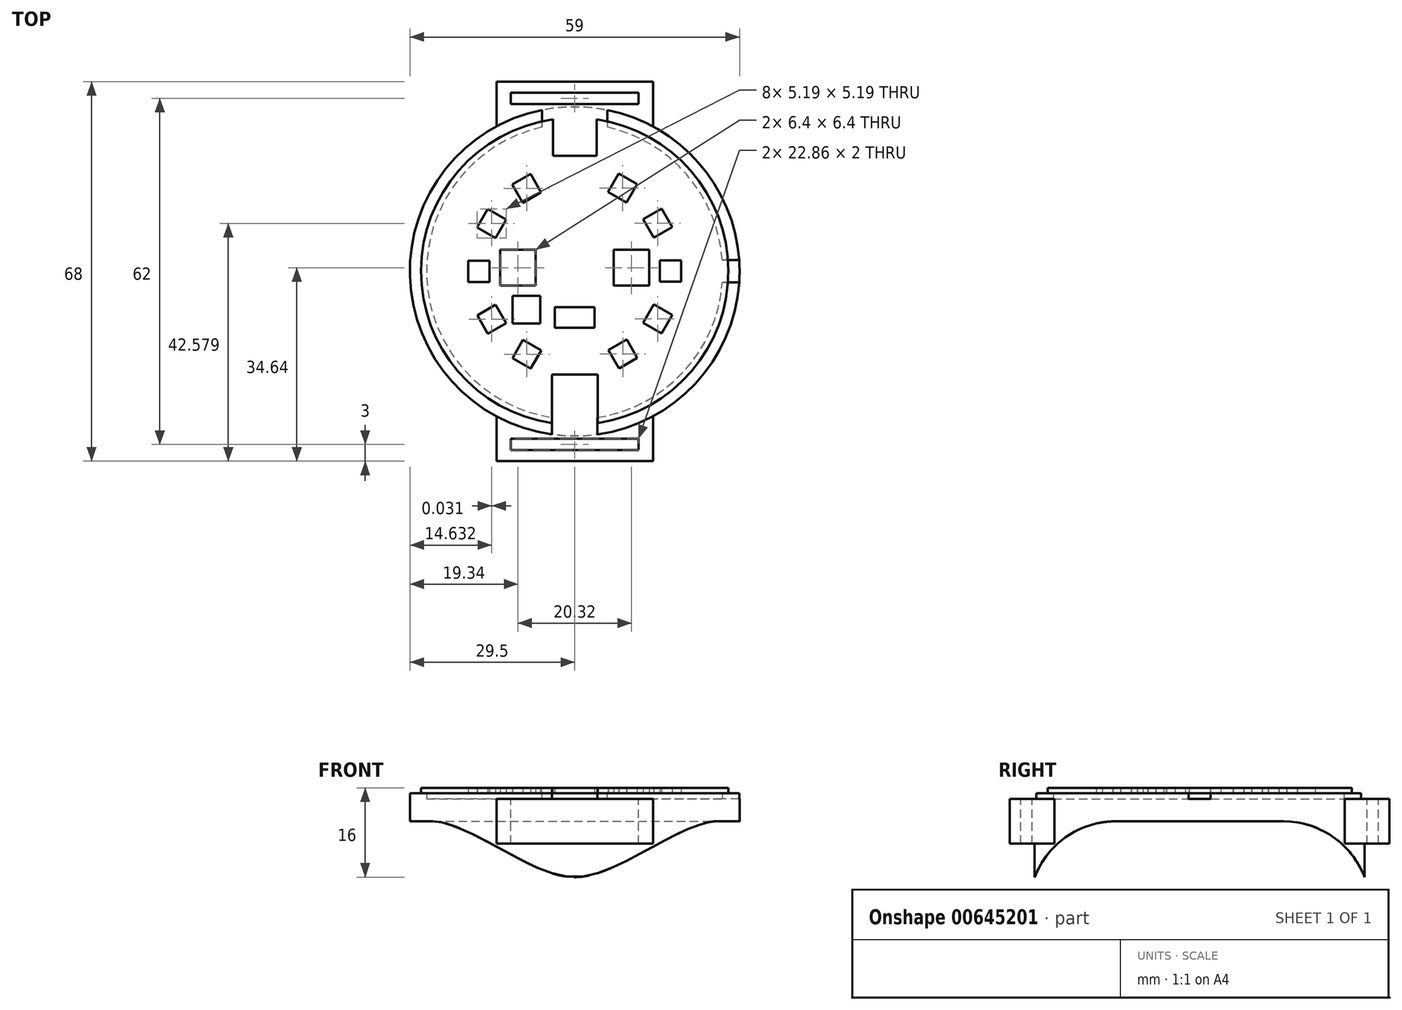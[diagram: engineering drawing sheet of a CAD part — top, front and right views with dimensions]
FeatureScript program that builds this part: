
annotation { "Feature Type Name" : "Feature", "Feature Type Description" : "" }
export const myFeature = defineFeature(function(context is Context, id is Id, definition is map)
    precondition{}
    {
        {
            var Q0;
            Q0=qCreatedBy(makeId("Top.planeOp"),FACE);
            var sketch = newSketch(context, id + "F0", { "sketchPlane" : qUnion([Q0])});
            skCircle(sketch, "E0", {"center": v(0, 0) * mm, "radius": 26.5 * mm});
            skCircle(sketch, "E1.0", {"center": v(0, 0) * mm, "radius": 29.5 * mm});
            skSolve(sketch);
        }
        {
            var Q0;
            Q0=makeQuery(id+"F0.imprint","IMPRINT",FACE,{"disambiguationData":[TD([[makeQuery(id+"F0.imprint","IMPRINT",EDGE,{"derivedFrom":sQuery(id+"F0.wireOp",EDGE,"E0")}),-1.0]])]});
            var Q1;
            Q1=makeQuery(id+"F0.imprint","IMPRINT",FACE,{"disambiguationData":[TD([[makeQuery(id+"F0.imprint","IMPRINT",EDGE,{"derivedFrom":sQuery(id+"F0.wireOp",EDGE,"E0")}),1.0]])]});
            var Q2;
            Q2 = qConstructionFilter(qBodyType(qCreatedBy(id + "F0" ,EDGE), BodyType.WIRE), ConstructionObject.NO);
            extrude(context, id + "F1", {"entities" : qUnion([Q0, Q1]), "surfaceEntities" : qUnion([Q2]), "oppositeDirection" : true, "depth" : 4 * mm, "offsetDistance" : 25 * mm});
        }
        {
            var Q0;
            Q0=makeQuery(id+"F1.opExtrude","CAP_FACE",FACE,{"disambiguationData":[OSD([sQuery(id+"F0.wireOp",EDGE,"E1.0")])],"isStart":false});
            var sketch = newSketch(context, id + "F2", { "sketchPlane" : qUnion([Q0])});
            skLineSegment(sketch, "E2", {"start": v(0, 29.5) * mm, "end": v(0, -29.5) * mm});
            skSolve(sketch);
        }
        {
            var Q0;
            Q0=makeQuery(id+"F0.imprint","IMPRINT",FACE,{"disambiguationData":[TD([[makeQuery(id+"F0.imprint","IMPRINT",EDGE,{"derivedFrom":sQuery(id+"F0.wireOp",EDGE,"E0")}),-1.0]])]});
            extrude(context, id + "F3", {"entities" : qUnion([Q0]), "operationType" : NewBodyOperationType.ADD, "depth" : 1 * mm, "offsetDistance" : 25 * mm});
        }
        {
            var Q0;
            Q0=qCreatedBy(makeId("Front.planeOp"),FACE);
            var sketch = newSketch(context, id + "F4", { "sketchPlane" : qUnion([Q0])});
            skLineSegment(sketch, "E3", {"start": v(0, 0) * mm, "end": v(-4.05, 0) * mm});
            skLineSegment(sketch, "E4.MirrorCS", {"start": v(0, 0) * mm, "end": v(4.05, 0) * mm});
            skLineSegment(sketch, "E5", {"start": v(-4.05, 0) * mm, "end": v(-4.05, 3) * mm});
            skLineSegment(sketch, "E6", {"start": v(-4.05, 3) * mm, "end": v(4.05, 3) * mm});
            skLineSegment(sketch, "E7", {"start": v(4.05, 3) * mm, "end": v(4.05, 0) * mm});
            skSolve(sketch);
        }
        {
            var Q0;
            Q0 = qSketchRegion(id + "F4", true);
            extrude(context, id + "F5", {"entities" : qUnion([Q0]), "operationType" : NewBodyOperationType.REMOVE, "endBound" : BoundingType.THROUGH_ALL, "depth" : 25 * mm, "offsetDistance" : 25 * mm});
        }
        {
            var Q0;
            Q0=qCreatedBy(makeId("Front.planeOp"),FACE);
            var sketch = newSketch(context, id + "F6", { "sketchPlane" : qUnion([Q0])});
            skLineSegment(sketch, "E8", {"start": v(0, 0) * mm, "end": v(-5.85, 0) * mm});
            skLineSegment(sketch, "E9.MirrorCS", {"start": v(0, 0) * mm, "end": v(5.85, 0) * mm});
            skLineSegment(sketch, "E10", {"start": v(-5.85, 0) * mm, "end": v(-5.85, 3) * mm});
            skLineSegment(sketch, "E11", {"start": v(-5.85, 3) * mm, "end": v(5.85, 3) * mm});
            skLineSegment(sketch, "E12", {"start": v(5.85, 3) * mm, "end": v(5.85, 0) * mm});
            skSolve(sketch);
        }
        {
            var Q0;
            Q0 = qSketchRegion(id + "F6", true);
            extrude(context, id + "F7", {"entities" : qUnion([Q0]), "operationType" : NewBodyOperationType.REMOVE, "endBound" : BoundingType.THROUGH_ALL, "oppositeDirection" : true, "depth" : 25 * mm, "offsetDistance" : 25 * mm});
        }
        {
            var Q0;
            Q0=qCreatedBy(makeId("Front.planeOp"),FACE);
            var sketch = newSketch(context, id + "F8", { "sketchPlane" : qUnion([Q0])});
            skLineSegment(sketch, "E13", {"start": v(0, 0) * mm, "end": v(-14, 0) * mm});
            skLineSegment(sketch, "E14.MirrorCS", {"start": v(0, 0) * mm, "end": v(14, 0) * mm});
            skLineSegment(sketch, "E15", {"start": v(-14, 0) * mm, "end": v(-14, -4) * mm});
            skLineSegment(sketch, "E16", {"start": v(-14, -4) * mm, "end": v(14, -4) * mm});
            skLineSegment(sketch, "E17", {"start": v(14, -4) * mm, "end": v(14, 0) * mm});
            skSolve(sketch);
        }
        {
            var Q0;
            Q0 = qSketchRegion(id + "F8", true);
            var Q1;
            {var subQ0=sQuery(id+"F0.wireOp",EDGE,"E1.0");Q1=makeQuery(id+"F3.boolean.opBoolean","MERGE",FACE,{"derivedFrom":[makeQuery(id+"F1.opExtrude","SWEPT_FACE",FACE,{"disambiguationData":[OSD([subQ0])]}),makeQuery(id+"F3.opExtrude","SWEPT_FACE",FACE,{"disambiguationData":[OSD([subQ0])]})]});}
            extrude(context, id + "F9", {"entities" : qUnion([Q0]), "operationType" : NewBodyOperationType.ADD, "endBound" : BoundingType.SYMMETRIC, "depth" : 68 * mm, "endBoundEntityFace" : qUnion([Q1]), "offsetDistance" : 25 * mm});
        }
        {
            var Q0;
            Q0=makeQuery(id+"F9.boolean.opBoolean","MERGE",FACE,{"derivedFrom":[makeQuery(id+"F7.boolean.opBoolean","MERGE",FACE,{"derivedFrom":[makeQuery(id+"F5.boolean.opBoolean","MERGE",FACE,{"derivedFrom":[makeQuery(id+"F1.opExtrude","CAP_FACE",FACE,{"disambiguationData":[OSD([sQuery(id+"F0.wireOp",EDGE,"E1.0")])],"isStart":true}),makeQuery(id+"F5.opExtrude","SWEPT_FACE",FACE,{"disambiguationData":[OSD([sQuery(id+"F4.wireOp",EDGE,"E3"),sQuery(id+"F4.wireOp",EDGE,"E4.MirrorCS")])]})]}),makeQuery(id+"F7.opExtrude","SWEPT_FACE",FACE,{"disambiguationData":[OSD([sQuery(id+"F6.wireOp",EDGE,"E8"),sQuery(id+"F6.wireOp",EDGE,"E9.MirrorCS")])]})]}),makeQuery(id+"F9.opExtrude","SWEPT_FACE",FACE,{"disambiguationData":[OSD([sQuery(id+"F8.wireOp",EDGE,"E13"),sQuery(id+"F8.wireOp",EDGE,"E14.MirrorCS")])]})]});
            var sketch = newSketch(context, id + "F10", { "sketchPlane" : qUnion([Q0])});
            skLineSegment(sketch, "E18", {"start": v(0, 0) * mm, "end": v(0, -31) * mm, "construction": true});
            skLineSegment(sketch, "E19.bottom", {"start": v(11.43, -30) * mm, "end": v(-11.43, -30) * mm});
            skLineSegment(sketch, "E19.top", {"start": v(11.43, -32) * mm, "end": v(-11.43, -32) * mm});
            skLineSegment(sketch, "E19.left", {"start": v(11.43, -30) * mm, "end": v(11.43, -32) * mm});
            skLineSegment(sketch, "E19.right", {"start": v(-11.43, -30) * mm, "end": v(-11.43, -32) * mm});
            skPoint(sketch, "E19.middle", {"position": v(0, -31) * mm});
            skLineSegment(sketch, "E20.MirrorCS", {"start": v(11.43, 32) * mm, "end": v(-11.43, 32) * mm});
            skLineSegment(sketch, "E21.MirrorCS", {"start": v(11.43, 30) * mm, "end": v(-11.43, 30) * mm});
            skLineSegment(sketch, "E22.MirrorCS", {"start": v(11.43, 30) * mm, "end": v(11.43, 32) * mm});
            skLineSegment(sketch, "E23.MirrorCS", {"start": v(-11.43, 30) * mm, "end": v(-11.43, 32) * mm});
            skSolve(sketch);
        }
        {
            var Q0;
            Q0=makeQuery(id+"F10.imprint","IMPRINT",FACE,{"disambiguationData":[TD([[makeQuery(id+"F10.imprint","IMPRINT",EDGE,{"derivedFrom":sQuery(id+"F10.wireOp",EDGE,"E20.MirrorCS")}),1.0]])]});
            var Q1;
            Q1=makeQuery(id+"F10.imprint","IMPRINT",FACE,{"disambiguationData":[TD([[makeQuery(id+"F10.imprint","IMPRINT",EDGE,{"derivedFrom":sQuery(id+"F10.wireOp",EDGE,"E19.bottom")}),1.0]])]});
            extrude(context, id + "F11", {"entities" : qUnion([Q0, Q1]), "operationType" : NewBodyOperationType.REMOVE, "endBound" : BoundingType.THROUGH_ALL, "oppositeDirection" : true, "depth" : 25 * mm, "offsetDistance" : 25 * mm});
        }
        {
            var Q0;
            Q0=qCreatedBy(makeId("Right.planeOp"),FACE);
            var sketch = newSketch(context, id + "F12", { "sketchPlane" : qUnion([Q0])});
            skLineSegment(sketch, "E24", {"start": v(0, 0) * mm, "end": v(-2, 0) * mm});
            skLineSegment(sketch, "E25", {"start": v(-2, 0) * mm, "end": v(-2, 3) * mm});
            skLineSegment(sketch, "E26", {"start": v(-2, 3) * mm, "end": v(0, 3) * mm});
            skLineSegment(sketch, "E27.MirrorCS", {"start": v(2, 0) * mm, "end": v(2, 3) * mm});
            skLineSegment(sketch, "E28.MirrorCS", {"start": v(0, 0) * mm, "end": v(2, 0) * mm});
            skLineSegment(sketch, "E29.MirrorCS", {"start": v(2, 3) * mm, "end": v(0, 3) * mm});
            skSolve(sketch);
        }
        {
            var Q0;
            Q0 = qSketchRegion(id + "F12", true);
            extrude(context, id + "F13", {"entities" : qUnion([Q0]), "operationType" : NewBodyOperationType.REMOVE, "endBound" : BoundingType.THROUGH_ALL, "depth" : 25 * mm, "offsetDistance" : 25 * mm});
        }
        {
            var Q0;
            {var subQ0=makeQuery(id+"F5.boolean.opBoolean","COPY",FACE,{"derivedFrom":makeQuery(id+"F5.opExtrude","SWEPT_FACE",FACE,{"disambiguationData":[OSD([sQuery(id+"F4.wireOp",EDGE,"E7")])]})});var subQ1=sQuery(id+"F0.wireOp",EDGE,"E0");var subQ3=sQuery(id+"F0.wireOp",EDGE,"E1.0");Q0=makeQuery(id+"F13.boolean.opBoolean","SPLIT",FACE,{"disambiguationData":[TD([subQ0])],"derivedFrom":makeQuery(id+"F7.boolean.opBoolean","SPLIT",FACE,{"disambiguationData":[TD([subQ0])],"derivedFrom":makeQuery(id+"F3.opExtrude","CAP_FACE",FACE,{"disambiguationData":[OSD([subQ1,subQ3])],"isStart":false})})});}
            var sketch = newSketch(context, id + "F14", { "sketchPlane" : qUnion([Q0])});
            skCircle(sketch, "E30", {"center": v(0, 0) * mm, "radius": 27.5 * mm});
            skSolve(sketch);
        }
        {
            var Q0;
            {var subQ0=sQuery(id+"F0.wireOp",EDGE,"E1.0");var subQ1=sQuery(id+"F0.wireOp",EDGE,"E0");Q0=makeQuery(id+"F7.boolean.opBoolean","SPLIT",FACE,{"disambiguationData":[TD([makeQuery(id+"F5.boolean.opBoolean","COPY",FACE,{"derivedFrom":makeQuery(id+"F5.opExtrude","SWEPT_FACE",FACE,{"disambiguationData":[OSD([sQuery(id+"F4.wireOp",EDGE,"E5")])]})})])],"derivedFrom":makeQuery(id+"F3.opExtrude","CAP_FACE",FACE,{"disambiguationData":[OSD([subQ1,subQ0])],"isStart":false})});}
            var sketch = newSketch(context, id + "F15", { "sketchPlane" : qUnion([Q0])});
            skLineSegment(sketch, "E31.bottom", {"start": v(-15.25, 1.9) * mm, "end": v(-19.05, 1.9) * mm});
            skLineSegment(sketch, "E31.top", {"start": v(-15.25, -1.9) * mm, "end": v(-19.05, -1.9) * mm});
            skLineSegment(sketch, "E31.left", {"start": v(-15.25, 1.9) * mm, "end": v(-15.25, -1.9) * mm});
            skLineSegment(sketch, "E31.right", {"start": v(-19.05, 1.9) * mm, "end": v(-19.05, -1.9) * mm});
            skPoint(sketch, "E31.middle", {"position": v(-17.15, 0) * mm});
            skLineSegment(sketch, "E32", {"start": v(0, 0) * mm, "end": v(0, 0.64) * mm, "construction": true});
            skLineSegment(sketch, "E33.bottom", {"start": v(-6.96, 3.84) * mm, "end": v(-13.36, 3.84) * mm});
            skLineSegment(sketch, "E33.top", {"start": v(-6.96, -2.56) * mm, "end": v(-13.36, -2.56) * mm});
            skLineSegment(sketch, "E33.left", {"start": v(-6.96, 3.84) * mm, "end": v(-6.96, -2.56) * mm});
            skLineSegment(sketch, "E33.right", {"start": v(-13.36, 3.84) * mm, "end": v(-13.36, -2.56) * mm});
            skPoint(sketch, "E33.middle", {"position": v(-10.16, 0.64) * mm});
            skLineSegment(sketch, "E34.bottom", {"start": v(-11.14, -4.36) * mm, "end": v(-6.14, -4.36) * mm});
            skLineSegment(sketch, "E34.top", {"start": v(-11.14, -9.36) * mm, "end": v(-6.14, -9.36) * mm});
            skLineSegment(sketch, "E34.left", {"start": v(-11.14, -4.36) * mm, "end": v(-11.14, -9.36) * mm});
            skLineSegment(sketch, "E34.right", {"start": v(-6.14, -4.36) * mm, "end": v(-6.14, -9.36) * mm});
            skPoint(sketch, "E34.middle", {"position": v(-8.64, -6.86) * mm});
            skLineSegment(sketch, "E35.bottom", {"start": v(3.55, -6.44) * mm, "end": v(-3.55, -6.44) * mm});
            skLineSegment(sketch, "E35.top", {"start": v(3.55, -10.09) * mm, "end": v(-3.55, -10.09) * mm});
            skLineSegment(sketch, "E35.left", {"start": v(3.55, -6.44) * mm, "end": v(3.55, -10.09) * mm});
            skLineSegment(sketch, "E35.right", {"start": v(-3.55, -6.44) * mm, "end": v(-3.55, -10.08) * mm});
            skPoint(sketch, "E35.middle", {"position": v(0, -8.26) * mm});
            skLineSegment(sketch, "E36.MirrorCS", {"start": v(6.96, 3.84) * mm, "end": v(13.36, 3.84) * mm});
            skLineSegment(sketch, "E37.MirrorCS", {"start": v(13.36, 3.84) * mm, "end": v(13.36, -2.56) * mm});
            skLineSegment(sketch, "E38.MirrorCS", {"start": v(6.96, -2.56) * mm, "end": v(13.36, -2.56) * mm});
            skLineSegment(sketch, "E39.MirrorCS", {"start": v(6.96, 3.84) * mm, "end": v(6.96, -2.56) * mm});
            skLineSegment(sketch, "E40.1.0", {"start": v(-17.43, -7.88) * mm, "end": v(-15.53, -11.17) * mm});
            skLineSegment(sketch, "E40.1.1", {"start": v(-12.24, -9.27) * mm, "end": v(-15.53, -11.17) * mm});
            skLineSegment(sketch, "E40.1.2", {"start": v(-14.14, -5.98) * mm, "end": v(-17.43, -7.88) * mm});
            skLineSegment(sketch, "E40.1.3", {"start": v(-14.14, -5.98) * mm, "end": v(-12.24, -9.27) * mm});
            skLineSegment(sketch, "E40.2.0", {"start": v(-11.14, -15.53) * mm, "end": v(-7.85, -17.43) * mm});
            skLineSegment(sketch, "E40.2.1", {"start": v(-5.95, -14.14) * mm, "end": v(-7.85, -17.43) * mm});
            skLineSegment(sketch, "E40.2.2", {"start": v(-9.24, -12.24) * mm, "end": v(-11.14, -15.53) * mm});
            skLineSegment(sketch, "E40.2.3", {"start": v(-9.24, -12.24) * mm, "end": v(-5.95, -14.14) * mm});
            skLineSegment(sketch, "E40.4.0", {"start": v(7.9, -17.4) * mm, "end": v(11.2, -15.5) * mm});
            skLineSegment(sketch, "E40.4.1", {"start": v(9.3, -12.21) * mm, "end": v(11.2, -15.5) * mm});
            skLineSegment(sketch, "E40.4.2", {"start": v(6, -14.11) * mm, "end": v(7.9, -17.4) * mm});
            skLineSegment(sketch, "E40.4.3", {"start": v(6, -14.11) * mm, "end": v(9.3, -12.21) * mm});
            skLineSegment(sketch, "E40.5.0", {"start": v(15.56, -11.11) * mm, "end": v(17.46, -7.82) * mm});
            skLineSegment(sketch, "E40.5.1", {"start": v(14.17, -5.92) * mm, "end": v(17.46, -7.82) * mm});
            skLineSegment(sketch, "E40.5.2", {"start": v(12.27, -9.21) * mm, "end": v(15.56, -11.11) * mm});
            skLineSegment(sketch, "E40.5.3", {"start": v(12.27, -9.21) * mm, "end": v(14.17, -5.92) * mm});
            skLineSegment(sketch, "E40.6.0", {"start": v(19.05, -1.84) * mm, "end": v(19.05, 1.96) * mm});
            skLineSegment(sketch, "E40.6.1", {"start": v(15.25, 1.96) * mm, "end": v(19.05, 1.96) * mm});
            skLineSegment(sketch, "E40.6.2", {"start": v(15.25, -1.84) * mm, "end": v(19.05, -1.84) * mm});
            skLineSegment(sketch, "E40.6.3", {"start": v(15.25, -1.84) * mm, "end": v(15.25, 1.96) * mm});
            skLineSegment(sketch, "E40.7.0", {"start": v(17.43, 7.94) * mm, "end": v(15.53, 11.23) * mm});
            skLineSegment(sketch, "E40.7.1", {"start": v(12.24, 9.33) * mm, "end": v(15.53, 11.23) * mm});
            skLineSegment(sketch, "E40.7.2", {"start": v(14.14, 6.04) * mm, "end": v(17.43, 7.94) * mm});
            skLineSegment(sketch, "E40.7.3", {"start": v(14.14, 6.04) * mm, "end": v(12.24, 9.33) * mm});
            skLineSegment(sketch, "E40.8.0", {"start": v(11.14, 15.6) * mm, "end": v(7.85, 17.5) * mm});
            skLineSegment(sketch, "E40.8.1", {"start": v(5.95, 14.2) * mm, "end": v(7.85, 17.5) * mm});
            skLineSegment(sketch, "E40.8.2", {"start": v(9.24, 12.3) * mm, "end": v(11.14, 15.6) * mm});
            skLineSegment(sketch, "E40.8.3", {"start": v(9.24, 12.3) * mm, "end": v(5.95, 14.2) * mm});
            skLineSegment(sketch, "E40.10.0", {"start": v(-7.9, 17.46) * mm, "end": v(-11.2, 15.56) * mm});
            skLineSegment(sketch, "E40.10.1", {"start": v(-9.3, 12.27) * mm, "end": v(-11.2, 15.56) * mm});
            skLineSegment(sketch, "E40.10.2", {"start": v(-6, 14.17) * mm, "end": v(-7.9, 17.46) * mm});
            skLineSegment(sketch, "E40.10.3", {"start": v(-6, 14.17) * mm, "end": v(-9.3, 12.27) * mm});
            skLineSegment(sketch, "E40.11.0", {"start": v(-15.56, 11.17) * mm, "end": v(-17.46, 7.88) * mm});
            skLineSegment(sketch, "E40.11.1", {"start": v(-14.17, 5.98) * mm, "end": v(-17.46, 7.88) * mm});
            skLineSegment(sketch, "E40.11.2", {"start": v(-12.27, 9.27) * mm, "end": v(-15.56, 11.17) * mm});
            skLineSegment(sketch, "E40.11.3", {"start": v(-12.27, 9.27) * mm, "end": v(-14.17, 5.98) * mm});
            skPoint(sketch, "E40.center", {"position": v(0, 0.03) * mm});
            skLineSegment(sketch, "E41.bottom", {"start": v(3.9, 28.7) * mm, "end": v(-3.9, 28.7) * mm});
            skLineSegment(sketch, "E41.top", {"start": v(3.9, 20.7) * mm, "end": v(-3.9, 20.7) * mm});
            skLineSegment(sketch, "E41.left", {"start": v(3.9, 28.7) * mm, "end": v(3.9, 20.7) * mm});
            skLineSegment(sketch, "E41.right", {"start": v(-3.9, 28.7) * mm, "end": v(-3.9, 20.7) * mm});
            skPoint(sketch, "E41.middle", {"position": v(0, 24.7) * mm});
            skLineSegment(sketch, "E42.bottom", {"start": v(4.1, -18.47) * mm, "end": v(-4.1, -18.47) * mm});
            skLineSegment(sketch, "E42.top", {"start": v(4.1, -29.32) * mm, "end": v(-4.1, -29.32) * mm});
            skLineSegment(sketch, "E42.left", {"start": v(4.1, -18.47) * mm, "end": v(4.1, -29.32) * mm});
            skLineSegment(sketch, "E42.right", {"start": v(-4.1, -18.47) * mm, "end": v(-4.1, -29.32) * mm});
            skPoint(sketch, "E42.middle", {"position": v(0, -23.9) * mm});
            skSolve(sketch);
        }
        {
            var Q0;
            Q0 = qSketchRegion(id + "F14", true);
            extrude(context, id + "F16", {"entities" : qUnion([Q0]), "depth" : 1 * mm, "offsetDistance" : 25 * mm});
        }
        {
            var Q0;
            Q0 = qSketchRegion(id + "F15", true);
            extrude(context, id + "F17", {"entities" : qUnion([Q0]), "operationType" : NewBodyOperationType.REMOVE, "depth" : 25 * mm, "offsetDistance" : 25 * mm});
        }
        {
            var Q0;
            Q0=makeQuery(id+"F1.opExtrude","CAP_FACE",FACE,{"disambiguationData":[OSD([sQuery(id+"F0.wireOp",EDGE,"E1.0")])],"isStart":false});
            var sketch = newSketch(context, id + "F18", { "sketchPlane" : qUnion([Q0])});
            skCircle(sketch, "E43", {"center": v(0, 0) * mm, "radius": 29.5 * mm});
            skSolve(sketch);
        }
        {
            var Q0;
            Q0 = qSketchRegion(id + "F18", true);
            extrude(context, id + "F19", {"entities" : qUnion([Q0]), "depth" : 10 * mm, "offsetDistance" : 25 * mm});
        }
        {
            var Q0;
            Q0=makeQuery(id+"F19.opExtrude","CAP_FACE",FACE,{"disambiguationData":[OSD([sQuery(id+"F18.wireOp",EDGE,"E43")])],"isStart":false});
            var sketch = newSketch(context, id + "F20", { "sketchPlane" : qUnion([Q0])});
            skLineSegment(sketch, "E44", {"start": v(0, -29.5) * mm, "end": v(0, 29.5) * mm});
            skSolve(sketch);
        }
        {
            var Q0;
            Q0=qCreatedBy(makeId("Right.planeOp"),FACE);
            var sketch = newSketch(context, id + "F21", { "sketchPlane" : qUnion([Q0])});
            skLineSegment(sketch, "E45", {"start": v(0, -6.88) * mm, "end": v(0, 0) * mm, "construction": true});
            skLineSegment(sketch, "E46", {"start": v(0, -14) * mm, "end": v(29.5, -14) * mm});
            skLineSegment(sketch, "E47.MirrorCS", {"start": v(0, -14) * mm, "end": v(-29.5, -14) * mm});
            skLineSegment(sketch, "E48", {"start": v(0, -4) * mm, "end": v(15, -4) * mm});
            skArc(sketch, "E49", {"start": v(29.5, -14) * mm, "mid": v(23.8, -6.74) * mm, "end": v(15, -4) * mm});
            skLineSegment(sketch, "E50.MirrorCS", {"start": v(0, -4) * mm, "end": v(-15, -4) * mm});
            skArc(sketch, "E51.MirrorCS", {"start": v(-29.5, -14) * mm, "mid": v(-23.8, -6.74) * mm, "end": v(-15, -4) * mm});
            skSolve(sketch);
        }
        {
            var Q0;
            Q0 = qSketchRegion(id + "F21", true);
            extrude(context, id + "F22", {"entities" : qUnion([Q0]), "operationType" : NewBodyOperationType.REMOVE, "endBound" : BoundingType.SYMMETRIC, "oppositeDirection" : true, "depth" : 100 * mm, "offsetDistance" : 25 * mm});
        }
        {
            var Q0;
            {var subQ1=sQuery(id+"F8.wireOp",EDGE,"E16");Q0=makeQuery(id+"F18.imprint","IMPRINT",FACE,{"disambiguationData":[TD([[makeQuery(id+"F18.imprint","IMPRINT",EDGE,{"derivedFrom":makeQuery(id+"F9.opExtrude","CAP_EDGE",EDGE,{"disambiguationData":[OSD([subQ1])],"isStart":true})}),1.0]])]});}
            extrude(context, id + "F23", {"entities" : qUnion([Q0]), "operationType" : NewBodyOperationType.ADD, "depth" : 4 * mm, "offsetDistance" : 25 * mm});
        }
        {
            var Q0;
            {var subQ4=sQuery(id+"F8.wireOp",EDGE,"E16");Q0=makeQuery(id+"F18.imprint","IMPRINT",FACE,{"disambiguationData":[TD([[makeQuery(id+"F18.imprint","IMPRINT",EDGE,{"derivedFrom":makeQuery(id+"F9.opExtrude","CAP_EDGE",EDGE,{"disambiguationData":[OSD([subQ4])],"isStart":false})}),-1.0]])]});}
            extrude(context, id + "F24", {"entities" : qUnion([Q0]), "operationType" : NewBodyOperationType.ADD, "depth" : 4 * mm, "offsetDistance" : 25 * mm});
        }
    });
